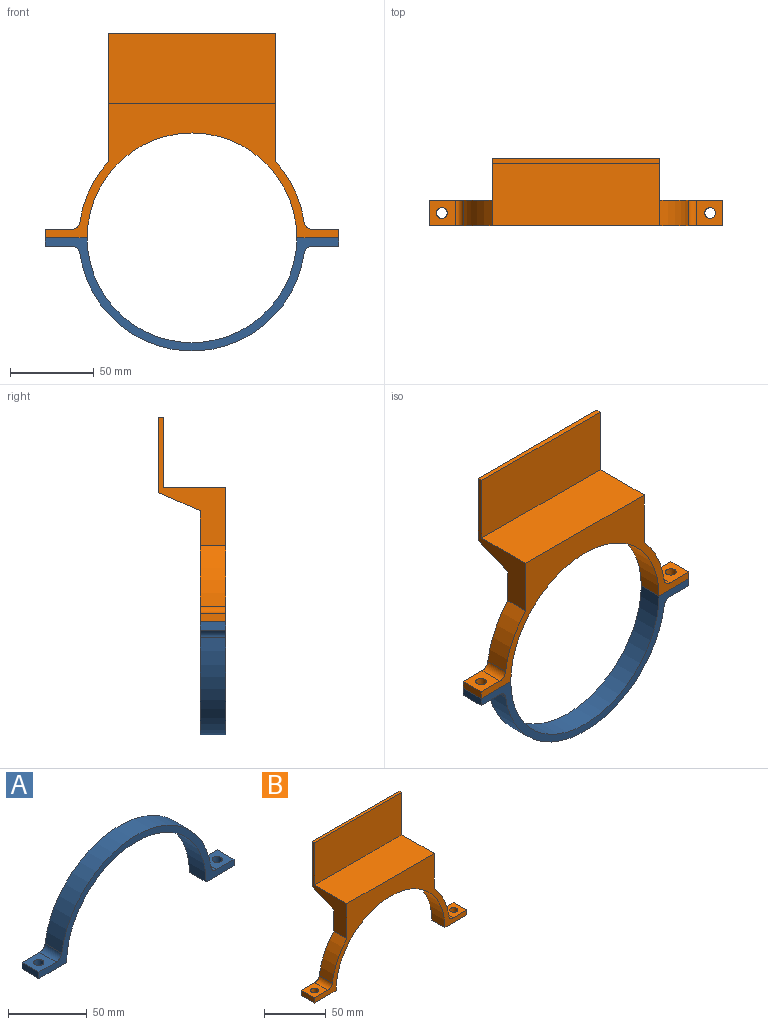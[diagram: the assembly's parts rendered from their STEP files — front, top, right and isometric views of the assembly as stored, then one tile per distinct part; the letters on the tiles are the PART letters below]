
ASSEMBLY  parts=2 mates=1
PART A: 14 faces, bbox 175x15x67.5 mm
  f0: cylinder r=67.5mm len=133.71mm, axis (0,1,0), area 2900.7mm2, adj f8,f9,f12,f13
  f1: plane 15.69x15mm, normal (0,0,1), area 202.2mm2, adj f2,f8,f9,f11,f12
  f2: plane 15x5mm, normal (-1,0,0), area 75mm2, adj f1,f3,f8,f9
  f3: plane 25x15mm, normal (0,0,-1), area 341.8mm2, adj f2,f4,f8,f9,f11
  f4: cylinder r=62.5mm len=125mm, axis (0,1,0), area 2945.2mm2, adj f3,f5,f8,f9
  f5: plane 25x15mm, normal (0,0,-1), area 341.8mm2, adj f4,f6,f8,f9,f10
  f6: plane 15x5mm, normal (1,0,0), area 75mm2, adj f5,f7,f8,f9
  f7: plane 15.69x15mm, normal (0,0,1), area 202.2mm2, adj f6,f8,f9,f10,f13
  f8: plane 175x67.5mm, normal (0,-1,0), area 1229.7mm2, adj f0,f1,f2,f3,f4,f5,f6,f7
  f9: plane 175x67.5mm, normal (0,1,0), area 1229.7mm2, adj f0,f1,f2,f3,f4,f5,f6,f7
  f10: cylinder r=3.25mm len=6.5mm, axis (0,0,1), area 102.1mm2, adj f5,f7
  f11: cylinder r=3.25mm len=6.5mm, axis (0,0,1), area 102.1mm2, adj f1,f3
  f12: cylinder r=5mm len=15mm, axis (0,1,0), area 107.4mm2, adj f0,f1,f8,f9
  f13: cylinder r=5mm len=15mm, axis (0,1,0), area 107.4mm2, adj f0,f7,f8,f9
PART B: 22 faces, bbox 175x40x122 mm
  f0: plane 175x66.21mm, normal (0,1,0), area 1782.4mm2, adj f1,f3,f5,f6,f7,f8,f9,f10
  f1: plane 76.65x40mm, normal (-1,0,0), area 855.7mm2, adj f0,f2,f4,f6,f18,f19,f20,f21
  f2: plane 175x80mm, normal (0,-1,0), area 3161.8mm2, adj f1,f3,f4,f5,f6,f7,f8,f9
  f3: plane 76.65x40mm, normal (1,0,0), area 855.7mm2, adj f0,f2,f4,f5,f18,f19,f20,f21
  f4: plane 100x37mm, normal (0,0,1), area 3700mm2, adj f1,f2,f3,f19
  f5: cylinder r=67.5mm len=36.04mm, axis (0,1,0), area 605.7mm2, adj f0,f2,f3,f17
  f6: cylinder r=67.5mm len=36.04mm, axis (0,1,0), area 605.7mm2, adj f0,f1,f2,f16
  f7: plane 15.69x15mm, normal (0,0,1), area 202.2mm2, adj f0,f2,f8,f15,f16
  f8: plane 15x5mm, normal (-1,0,0), area 75mm2, adj f0,f2,f7,f9
  f9: plane 25x15mm, normal (0,0,-1), area 341.8mm2, adj f0,f2,f8,f10,f15
  f10: cylinder r=62.5mm len=125mm, axis (0,1,0), area 2945.2mm2, adj f0,f2,f9,f11
  f11: plane 25x15mm, normal (0,0,-1), area 341.8mm2, adj f0,f2,f10,f12,f14
  f12: plane 15x5mm, normal (1,0,0), area 75mm2, adj f0,f2,f11,f13
  f13: plane 15.69x15mm, normal (0,0,1), area 202.2mm2, adj f0,f2,f12,f14,f17
  f14: cylinder r=3.25mm len=6.5mm, axis (0,0,1), area 102.1mm2, adj f11,f13
  f15: cylinder r=3.25mm len=6.5mm, axis (0,0,1), area 102.1mm2, adj f7,f9
  f16: cylinder r=5mm len=15mm, axis (0,1,0), area 107.4mm2, adj f0,f2,f6,f7
  f17: cylinder r=5mm len=15mm, axis (0,1,0), area 107.4mm2, adj f0,f2,f5,f13
  f18: plane 100x45mm, normal (0,1,0), area 4500mm2, adj f1,f3,f20,f21
  f19: plane 100x42mm, normal (0,-1,0), area 4200mm2, adj f1,f3,f4,f20
  f20: plane 100x3mm, normal (0,0,1), area 300mm2, adj f1,f3,f18,f19
  f21: plane 100x25mm, normal (0,0.4,-0.92), area 2723.1mm2, adj f0,f1,f3,f18
PLACE A rot(axis=(1,0,0),180deg) t=(6.03,28.96,4.46)mm
PLACE B t=(6.03,28.96,4.46)mm
MATE fastened A.f3 <-> B.f9  axis (0,0,1) through (-68.48,28.96,4.46)mm
